# Revit family: Shower_Kit-American_Standard-Spectra-1660771_Series
name_source: partatom
category: Plumbing Fixtures
units: mm (PartAtom-declared; Revit-internal decimal feet)

## family parameters
Cut with Voids When Loaded = No
Host = Face
OmniClass Number = 23.45.05.14.17
OmniClass Title = Showers
Part Type = Normal
Room Calculation Point = No
Round Connector Dimension = Use Diameter
Shared = Yes

## types (3) — shared parameters
Assembly Code = D2010710
CW Connection = No
CWFU = 3
CalGreen Compliant = Yes
Default Elevation = 60"
Description = Spectra® Handheld 1.8 gpm/6.8 L/min 4-Function Hand Shower Kit
EPA WaterSense® Certified = Yes
HW Connection = No
HWFU = 3
Hose - 8888.035 = Yes
IAPMO Compliance = ASME A112.18.1 and CSA B125.1
Installation Type = Wall Mounted
Length = 37 7/8"
Manufacturer = American Standard
Price = Prices may vary. Please consult Manufacturer Representative for most up-to-date price list.
Product Documentation Link = https://americanstandard.box.com
Product Page URL = https://www.americanstandard-us.com
Revised Date = 08/04/2022
Shower Arm Bracket - 8888.096 = Yes
Spectra+ Handheld - 9038.154 = Yes
Tempered Water Connection = Yes
Tempered Water Connection Diameter = 1/2"
Tempered Water Connection Radius = 1/4"
URL = https://www.americanstandard-us.com
Vent Connection = No
WFU = 4
Warranty Information = One Year General Product Warranty
Waste Connection = No
Width = 4 15/16"
cUPC Compliant = Yes

## per-type parameters (varying)
| type | Finish | Material |
| 1660771.002 | Metal-American Standard-002-Polished Chrome | Metal-American Standard-002-Polished Chrome |
| 1660771.295 | Metal-American Standard-002-Polished Chrome | Metal-American Standard-295-Brushed Nickel |
| 1660771.278 | Metal-American Standard-278-Legacy Bronze | Metal-American Standard-278-Legacy Bronze |

note: column(s) folded — value = type name in every type: Model

## geometry (parser evidence)
native form markers: Sweep x2
no freeform markers — native parametric forms only
